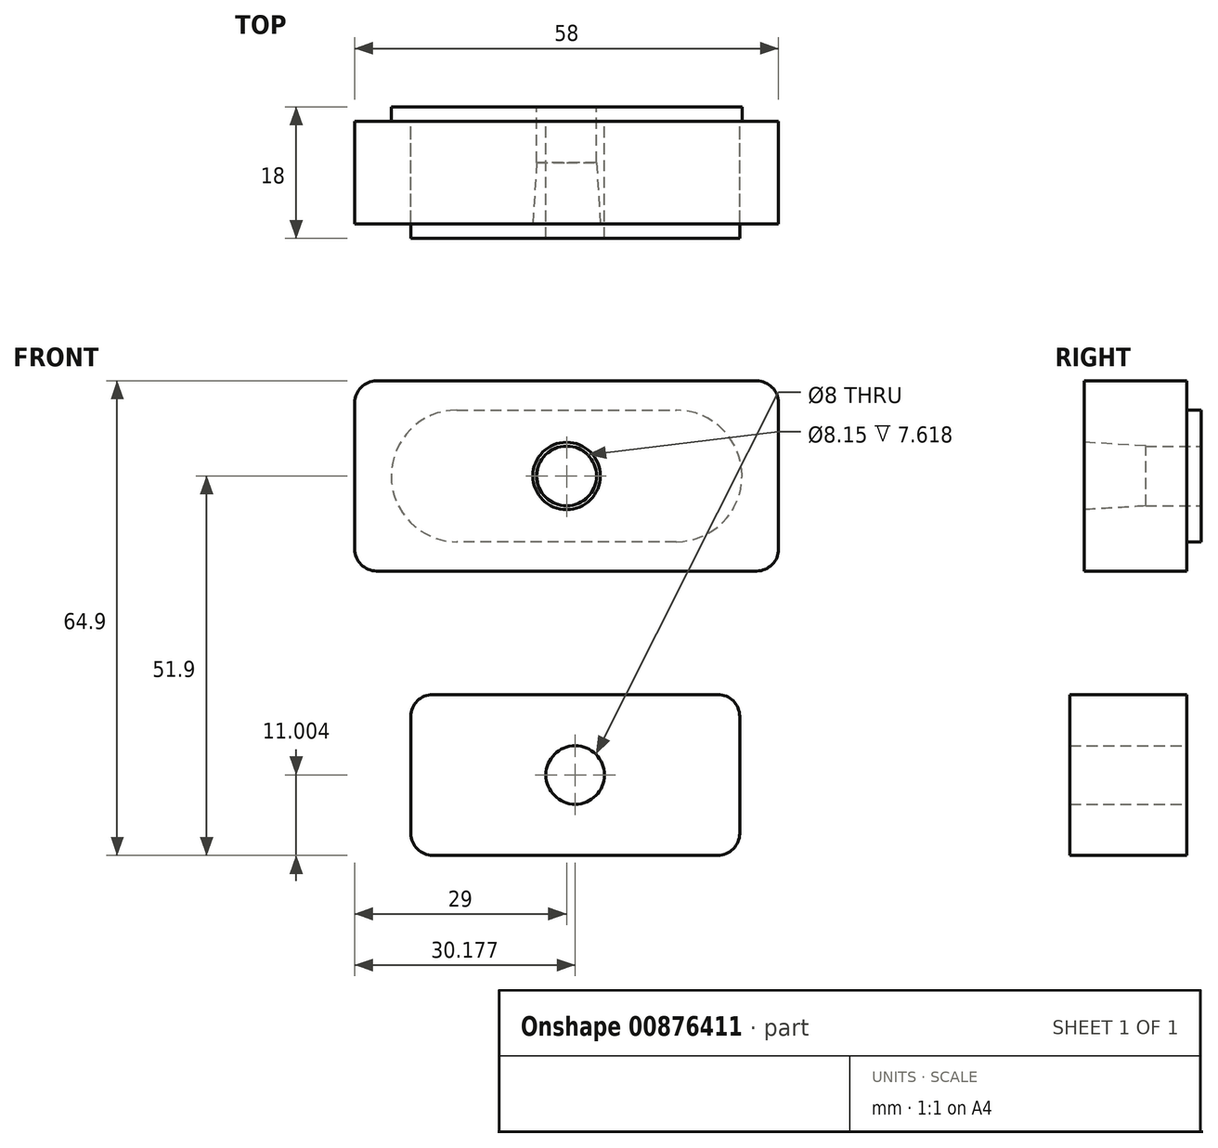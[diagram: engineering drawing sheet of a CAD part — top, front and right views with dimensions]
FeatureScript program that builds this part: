
annotation { "Feature Type Name" : "Feature", "Feature Type Description" : "" }
export const myFeature = defineFeature(function(context is Context, id is Id, definition is map)
    precondition{}
    {
        {
            var Q0;
            Q0=qCreatedBy(makeId("Front.planeOp"),FACE);
            var sketch = newSketch(context, id + "F0", { "sketchPlane" : qUnion([Q0])});
            skArc(sketch, "E0", {"start": v(-15, 9) * mm, "mid": v(-24, 0) * mm, "end": v(-15, -9) * mm});
            skArc(sketch, "E1", {"start": v(15, -9) * mm, "mid": v(24, 0) * mm, "end": v(15, 9) * mm});
            skLineSegment(sketch, "E2", {"start": v(-15, 9) * mm, "end": v(15, 9) * mm});
            skLineSegment(sketch, "E3", {"start": v(15, -9) * mm, "end": v(-15, -9) * mm});
            skLineSegment(sketch, "E4.bottom", {"start": v(29, -13) * mm, "end": v(-29, -13) * mm});
            skLineSegment(sketch, "E4.top", {"start": v(29, 13) * mm, "end": v(-29, 13) * mm});
            skLineSegment(sketch, "E4.left", {"start": v(29, -13) * mm, "end": v(29, 13) * mm});
            skLineSegment(sketch, "E4.right", {"start": v(-29, -13) * mm, "end": v(-29, 13) * mm});
            skPoint(sketch, "E4.middle", {"position": v(0, 0) * mm});
            skCircle(sketch, "E5", {"center": v(0, 0) * mm, "radius": 4.08 * mm});
            skSolve(sketch);
        }
        {
            var Q0;
            Q0=makeQuery(id+"F0.imprint","IMPRINT",FACE,{"disambiguationData":[TD([[makeQuery(id+"F0.imprint","IMPRINT",EDGE,{"derivedFrom":sQuery(id+"F0.wireOp",EDGE,"E0")}),-1.0]])]});
            var Q1;
            Q1=makeQuery(id+"F0.imprint","IMPRINT",FACE,{"disambiguationData":[TD([[makeQuery(id+"F0.imprint","IMPRINT",EDGE,{"derivedFrom":sQuery(id+"F0.wireOp",EDGE,"E0")}),1.0]])]});
            extrude(context, id + "F1", {"entities" : qUnion([Q0, Q1]), "depth" : 14 * mm, "offsetDistance" : 25 * mm});
        }
        {
            var Q0;
            Q0=makeQuery(id+"F0.imprint","IMPRINT",FACE,{"disambiguationData":[TD([[makeQuery(id+"F0.imprint","IMPRINT",EDGE,{"derivedFrom":sQuery(id+"F0.wireOp",EDGE,"E0")}),1.0]])]});
            extrude(context, id + "F2", {"entities" : qUnion([Q0]), "operationType" : NewBodyOperationType.ADD, "oppositeDirection" : true, "depth" : 2 * mm, "offsetDistance" : 25 * mm});
        }
        {
            var Q0;
            Q0=makeQuery(id+"F1.opExtrude","CAP_FACE",FACE,{"disambiguationData":[OSD([sQuery(id+"F0.wireOp",EDGE,"E4.bottom"),sQuery(id+"F0.wireOp",EDGE,"E4.top"),sQuery(id+"F0.wireOp",EDGE,"E4.left"),sQuery(id+"F0.wireOp",EDGE,"E4.right"),sQuery(id+"F0.wireOp",EDGE,"E5")])],"isStart":false});
            var sketch = newSketch(context, id + "F3", { "sketchPlane" : qUnion([Q0])});
            skCircle(sketch, "E6", {"center": v(0, 0) * mm, "radius": 4.61 * mm});
            skSolve(sketch);
        }
        {
            var Q0;
            Q0=makeQuery(id+"F3.imprint","IMPRINT",FACE,{"disambiguationData":[TD([[makeQuery(id+"F3.imprint","IMPRINT",EDGE,{"derivedFrom":sQuery(id+"F3.wireOp",EDGE,"E6")}),1.0]])]});
            var Q1;
            Q1=makeQuery(id+"F3.imprint","IMPRINT",FACE,{"disambiguationData":[TD([[makeQuery(id+"F3.imprint","IMPRINT",EDGE,{"derivedFrom":makeQuery(id+"F1.opExtrude","CAP_EDGE",EDGE,{"disambiguationData":[OSD([sQuery(id+"F0.wireOp",EDGE,"E5")])],"isStart":false})}),1.0]])]});
            extrude(context, id + "F4", {"entities" : qUnion([Q0, Q1]), "operationType" : NewBodyOperationType.REMOVE, "oppositeDirection" : true, "depth" : 8.38 * mm, "offsetDistance" : 25 * mm, "hasDraft" : true, "draftAngle" : 3.5 * degree, "draftPullDirection" : true});
        }
        {
            var Q0;
            Q0=makeQuery(id+"F1.opExtrude","SWEPT_EDGE",EDGE,{"disambiguationData":[OSD([sQuery(id+"F0.wireOp",EDGE,"E4.top"),sQuery(id+"F0.wireOp",EDGE,"E4.left")])]});
            var Q1;
            Q1=makeQuery(id+"F1.opExtrude","SWEPT_EDGE",EDGE,{"disambiguationData":[OSD([sQuery(id+"F0.wireOp",EDGE,"E4.bottom"),sQuery(id+"F0.wireOp",EDGE,"E4.left")])]});
            var Q2;
            Q2=makeQuery(id+"F1.opExtrude","SWEPT_EDGE",EDGE,{"disambiguationData":[OSD([sQuery(id+"F0.wireOp",EDGE,"E4.top"),sQuery(id+"F0.wireOp",EDGE,"E4.right")])]});
            var Q3;
            Q3=makeQuery(id+"F1.opExtrude","SWEPT_EDGE",EDGE,{"disambiguationData":[OSD([sQuery(id+"F0.wireOp",EDGE,"E4.bottom"),sQuery(id+"F0.wireOp",EDGE,"E4.right")])]});
            fillet(context, id + "F5", {"entities" : qUnion([Q0, Q1, Q2, Q3]), "tangentPropagation" : true, "radius" : 3 * mm, "defaultsChanged" : true, "vertexSettings" : [], "allowEdgeOverflow" : false});
        }
        {
            var Q0;
            Q0=qCreatedBy(makeId("Front.planeOp"),FACE);
            var sketch = newSketch(context, id + "F6", { "sketchPlane" : qUnion([Q0])});
            skLineSegment(sketch, "E7.bottom", {"start": v(23.68, -51.9) * mm, "end": v(-21.32, -51.9) * mm});
            skLineSegment(sketch, "E7.top", {"start": v(23.68, -29.9) * mm, "end": v(-21.32, -29.9) * mm});
            skLineSegment(sketch, "E7.left", {"start": v(23.68, -51.9) * mm, "end": v(23.68, -29.9) * mm});
            skLineSegment(sketch, "E7.right", {"start": v(-21.32, -51.9) * mm, "end": v(-21.32, -29.9) * mm});
            skPoint(sketch, "E7.middle", {"position": v(1.18, -40.9) * mm});
            skCircle(sketch, "E8", {"center": v(1.18, -40.9) * mm, "radius": 4 * mm});
            skSolve(sketch);
        }
        {
            var Q0;
            Q0=makeQuery(id+"F6.imprint","IMPRINT",FACE,{"disambiguationData":[TD([[makeQuery(id+"F6.imprint","IMPRINT",EDGE,{"derivedFrom":sQuery(id+"F6.wireOp",EDGE,"E7.bottom")}),-1.0]])]});
            extrude(context, id + "F7", {"entities" : qUnion([Q0]), "depth" : 16 * mm, "offsetDistance" : 25 * mm});
        }
        {
            var Q0;
            Q0=makeQuery(id+"F7.opExtrude","SWEPT_EDGE",EDGE,{"disambiguationData":[OSD([sQuery(id+"F6.wireOp",EDGE,"E7.top"),sQuery(id+"F6.wireOp",EDGE,"E7.left")])]});
            var Q1;
            Q1=makeQuery(id+"F7.opExtrude","SWEPT_EDGE",EDGE,{"disambiguationData":[OSD([sQuery(id+"F6.wireOp",EDGE,"E7.bottom"),sQuery(id+"F6.wireOp",EDGE,"E7.left")])]});
            var Q2;
            Q2=makeQuery(id+"F7.opExtrude","SWEPT_EDGE",EDGE,{"disambiguationData":[OSD([sQuery(id+"F6.wireOp",EDGE,"E7.top"),sQuery(id+"F6.wireOp",EDGE,"E7.right")])]});
            var Q3;
            Q3=makeQuery(id+"F7.opExtrude","SWEPT_EDGE",EDGE,{"disambiguationData":[OSD([sQuery(id+"F6.wireOp",EDGE,"E7.bottom"),sQuery(id+"F6.wireOp",EDGE,"E7.right")])]});
            fillet(context, id + "F8", {"entities" : qUnion([Q0, Q1, Q2, Q3]), "tangentPropagation" : true, "radius" : 3 * mm, "defaultsChanged" : true, "vertexSettings" : [], "allowEdgeOverflow" : false});
        }
    });
